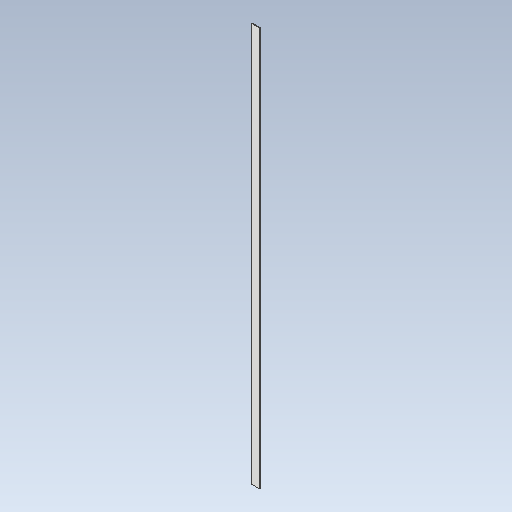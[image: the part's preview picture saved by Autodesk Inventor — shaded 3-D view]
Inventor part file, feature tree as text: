
AUTODESK INVENTOR PART (.ipt)
format: ipt  version: 2020.1 (Build 241239000, 239)  size: 103,424 bytes
history: native  units: mm
features: sheet_metal_op x1, sketch x1, other x1
ambient origin geometry x8: Origin, YZ Plane, XZ Plane, XY Plane, X Axis, Y Axis, Z Axis, Center Point
bodies: Solid1 (feature_tree)
feature tree (3):
  sheet_metal_op  "Face1"
  sketch  "Sketch1"  dims[d0=24.0mm d1=1208.0mm d2=2.0mm]
  other  "Plate1"
